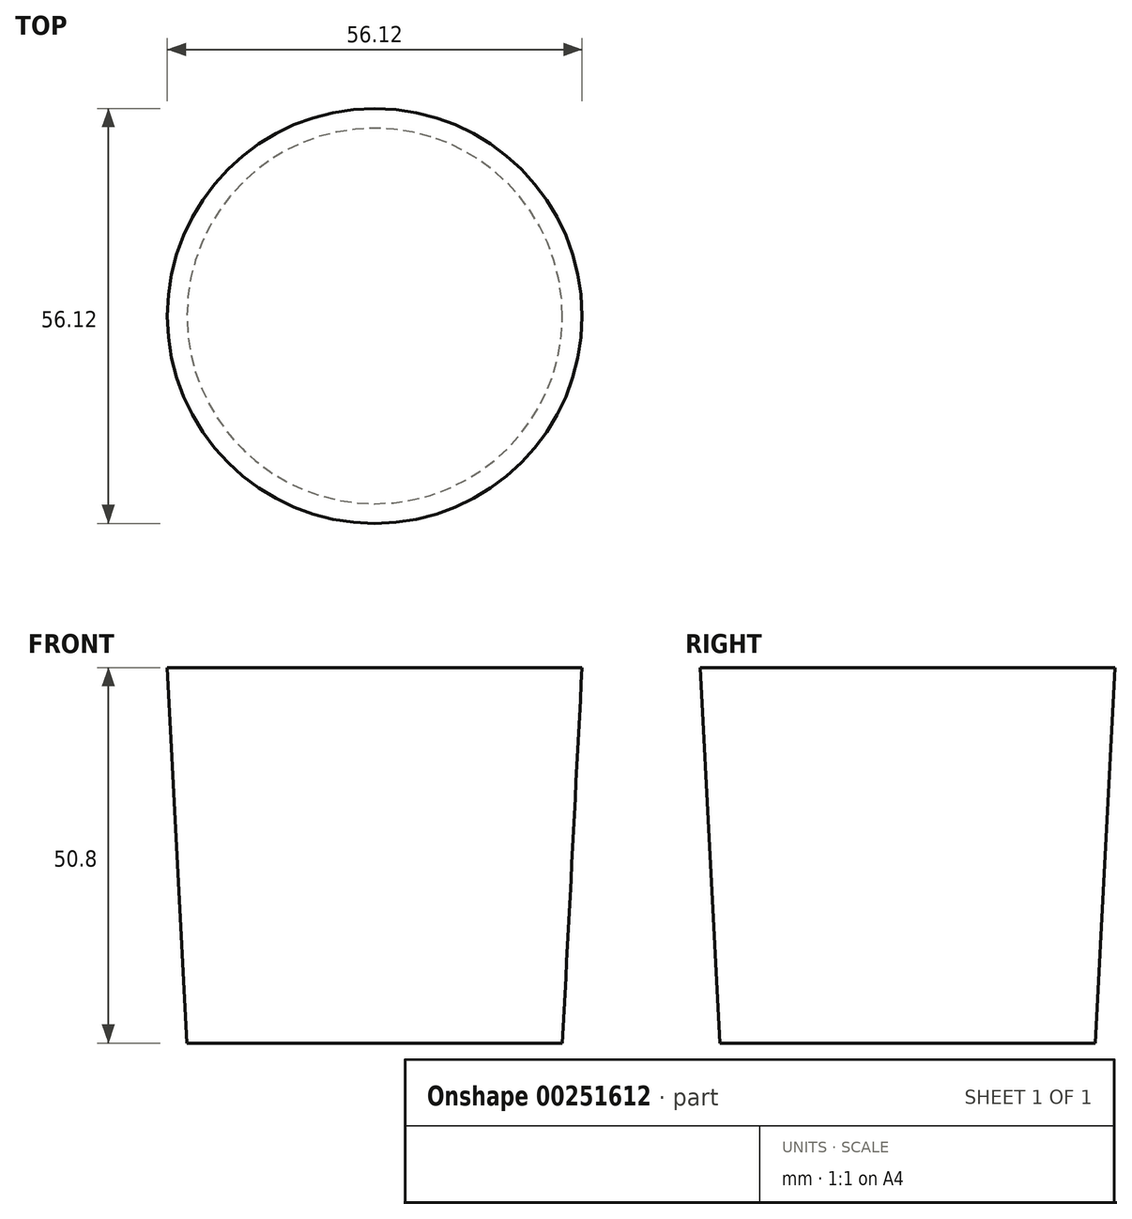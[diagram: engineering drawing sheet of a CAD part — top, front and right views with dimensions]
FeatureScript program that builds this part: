
annotation { "Feature Type Name" : "Feature", "Feature Type Description" : "" }
export const myFeature = defineFeature(function(context is Context, id is Id, definition is map)
    precondition{}
    {
        {
            var Q0;
            Q0=qCreatedBy(makeId("Top.planeOp"),FACE);
            var sketch = newSketch(context, id + "F0", { "sketchPlane" : qUnion([Q0])});
            skCircle(sketch, "E0", {"center": v(0, 0) * mm, "radius": 25.4 * mm});
            skSolve(sketch);
        }
        {
            var Q0;
            Q0 = qSketchRegion(id + "F0", true);
            extrude(context, id + "F1", {"entities" : qUnion([Q0]), "depth" : 50.8 * mm, "hasDraft" : true, "draftAngle" : 3 * degree});
        }
    });
